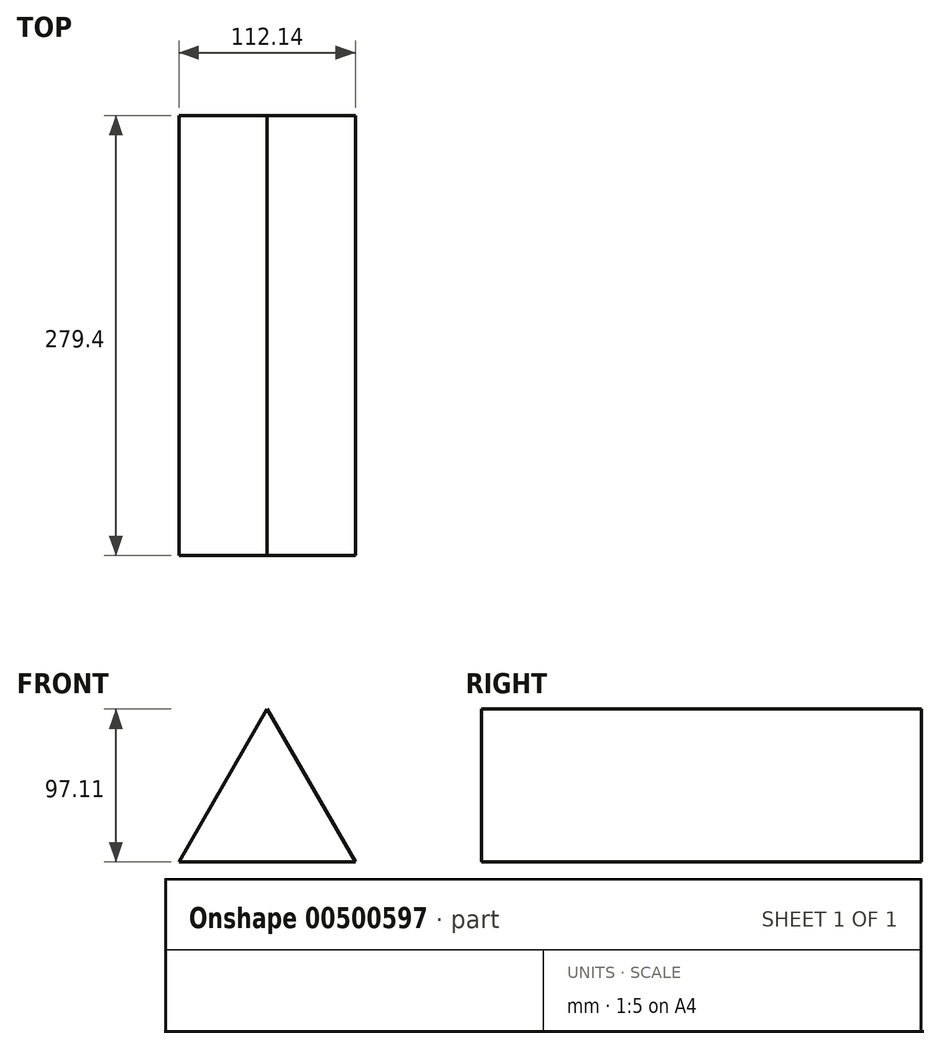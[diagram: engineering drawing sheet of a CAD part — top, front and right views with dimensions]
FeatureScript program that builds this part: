
annotation { "Feature Type Name" : "Feature", "Feature Type Description" : "" }
export const myFeature = defineFeature(function(context is Context, id is Id, definition is map)
    precondition{}
    {
        {
            var Q0;
            Q0=qCreatedBy(makeId("Front.planeOp"),FACE);
            var sketch = newSketch(context, id + "F0", { "sketchPlane" : qUnion([Q0])});
            skCircle(sketch, "E0.cCircle", {"center": v(0, 4.62) * mm, "radius": 64.74 * mm, "construction": true});
            skLineSegment(sketch, "E0.0", {"start": v(56.07, -27.75) * mm, "end": v(-56.07, -27.75) * mm});
            skLineSegment(sketch, "E0.1", {"start": v(-56.07, -27.75) * mm, "end": v(0, 69.36) * mm});
            skLineSegment(sketch, "E0.2", {"start": v(0, 69.36) * mm, "end": v(56.07, -27.75) * mm});
            skSolve(sketch);
        }
        {
            var Q0;
            Q0 = qSketchRegion(id + "F0", true);
            extrude(context, id + "F1", {"entities" : qUnion([Q0]), "depth" : 279.4 * mm});
        }
    });
